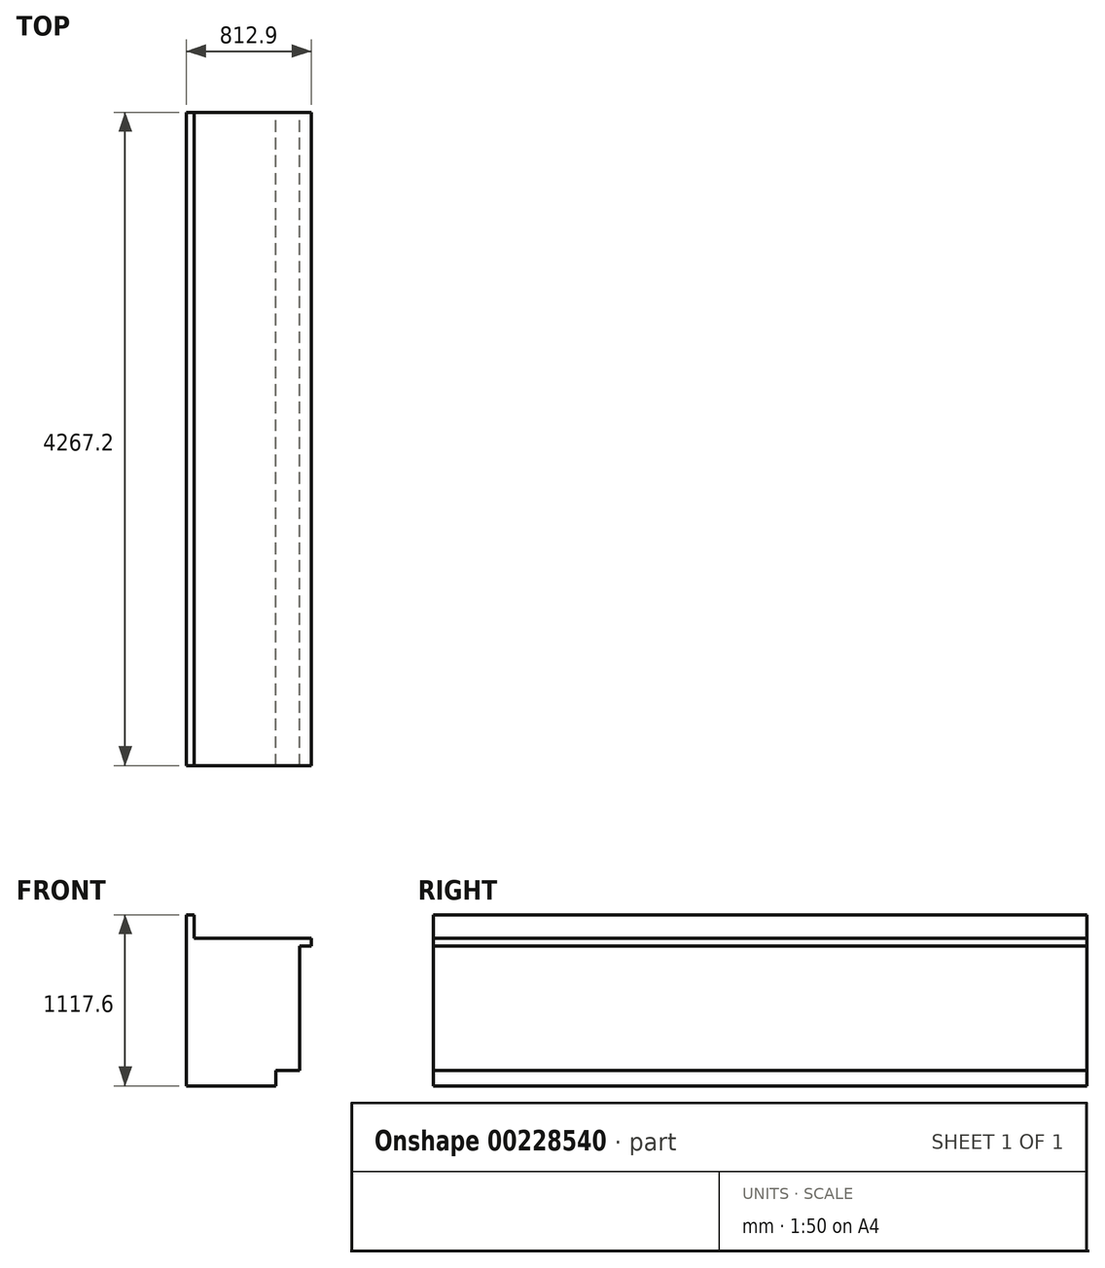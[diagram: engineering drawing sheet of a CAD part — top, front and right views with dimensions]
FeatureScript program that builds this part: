
annotation { "Feature Type Name" : "Feature", "Feature Type Description" : "" }
export const myFeature = defineFeature(function(context is Context, id is Id, definition is map)
    precondition{}
    {
        {
            var Q0;
            Q0=qCreatedBy(makeId("Top.planeOp"),FACE);
            var sketch = newSketch(context, id + "F0", { "sketchPlane" : qUnion([Q0])});
            skLineSegment(sketch, "E0", {"start": v(0, 0) * mm, "end": v(8161.31, 2103.83) * mm, "construction": true});
            skLineSegment(sketch, "E1.MirrorCS", {"start": v(0, 0) * mm, "end": v(8161.31, -2103.83) * mm, "construction": true});
            skArc(sketch, "E2", {"start": v(8161.31, 2103.83) * mm, "mid": v(-8428.11, 0) * mm, "end": v(8161.31, -2103.83) * mm, "construction": true});
            skArc(sketch, "E3", {"start": v(8161.31, -2103.83) * mm, "mid": v(8428.11, 0) * mm, "end": v(8161.31, 2103.83) * mm});
            skLineSegment(sketch, "E4.bottom", {"start": v(5570.51, 2103.83) * mm, "end": v(6332.51, 2103.83) * mm});
            skLineSegment(sketch, "E4.top", {"start": v(5570.51, -2103.83) * mm, "end": v(6332.51, -2103.83) * mm});
            skLineSegment(sketch, "E4.left", {"start": v(5570.51, 2103.83) * mm, "end": v(5570.51, -2103.83) * mm});
            skLineSegment(sketch, "E4.right", {"start": v(6332.51, 2103.83) * mm, "end": v(6332.51, -2103.83) * mm});
            skArc(sketch, "E5", {"start": v(8887.4, 2103.83) * mm, "mid": v(-9133.02, 0) * mm, "end": v(8887.4, -2103.83) * mm, "construction": true});
            skArc(sketch, "E6", {"start": v(8887.4, -2103.83) * mm, "mid": v(9133.02, 0) * mm, "end": v(8887.4, 2103.83) * mm});
            skLineSegment(sketch, "E7", {"start": v(8161.31, 2103.83) * mm, "end": v(8887.4, 2103.83) * mm});
            skLineSegment(sketch, "E8", {"start": v(8161.31, -2103.83) * mm, "end": v(8887.4, -2103.83) * mm});
            skSolve(sketch);
        }
        {
            var Q0;
            Q0=qCreatedBy(makeId("Front.planeOp"),FACE);
            var sketch = newSketch(context, id + "F1", { "sketchPlane" : qUnion([Q0])});
            skLineSegment(sketch, "E9.bottom", {"start": v(5570.51, 0) * mm, "end": v(6154.81, 0) * mm});
            skLineSegment(sketch, "E9.top", {"start": v(5621.31, 965.2) * mm, "end": v(6332.51, 965.2) * mm});
            skLineSegment(sketch, "E9.left", {"start": v(5570.51, 0) * mm, "end": v(5570.51, 965.2) * mm});
            skLineSegment(sketch, "E10", {"start": v(5570.51, 1117.6) * mm, "end": v(5621.31, 1117.6) * mm});
            skLineSegment(sketch, "E11", {"start": v(5621.31, 1117.6) * mm, "end": v(5621.31, 965.2) * mm});
            skLineSegment(sketch, "E12", {"start": v(5570.51, 965.2) * mm, "end": v(5570.51, 1117.6) * mm});
            skLineSegment(sketch, "E13", {"start": v(6332.51, 965.2) * mm, "end": v(6383.41, 965.2) * mm});
            skLineSegment(sketch, "E14", {"start": v(6383.41, 965.2) * mm, "end": v(6383.41, 914.3) * mm});
            skLineSegment(sketch, "E15", {"start": v(6383.41, 914.3) * mm, "end": v(6307.21, 914.3) * mm});
            skLineSegment(sketch, "E16", {"start": v(6307.21, 914.3) * mm, "end": v(6307.21, 101.6) * mm});
            skLineSegment(sketch, "E17", {"start": v(6307.21, 101.6) * mm, "end": v(6154.81, 101.6) * mm});
            skLineSegment(sketch, "E18", {"start": v(6154.81, 101.6) * mm, "end": v(6154.81, 0) * mm});
            skSolve(sketch);
        }
        {
            var Q0;
            Q0=makeQuery(id+"F1.imprint","IMPRINT",FACE,{"disambiguationData":[TD([[makeQuery(id+"F1.imprint","IMPRINT",EDGE,{"derivedFrom":sQuery(id+"F1.wireOp",EDGE,"E9.bottom")}),1.0]])]});
            extrude(context, id + "F2", {"entities" : qUnion([Q0]), "endBound" : BoundingType.SYMMETRIC, "depth" : 4267.2 * mm});
        }
    });
